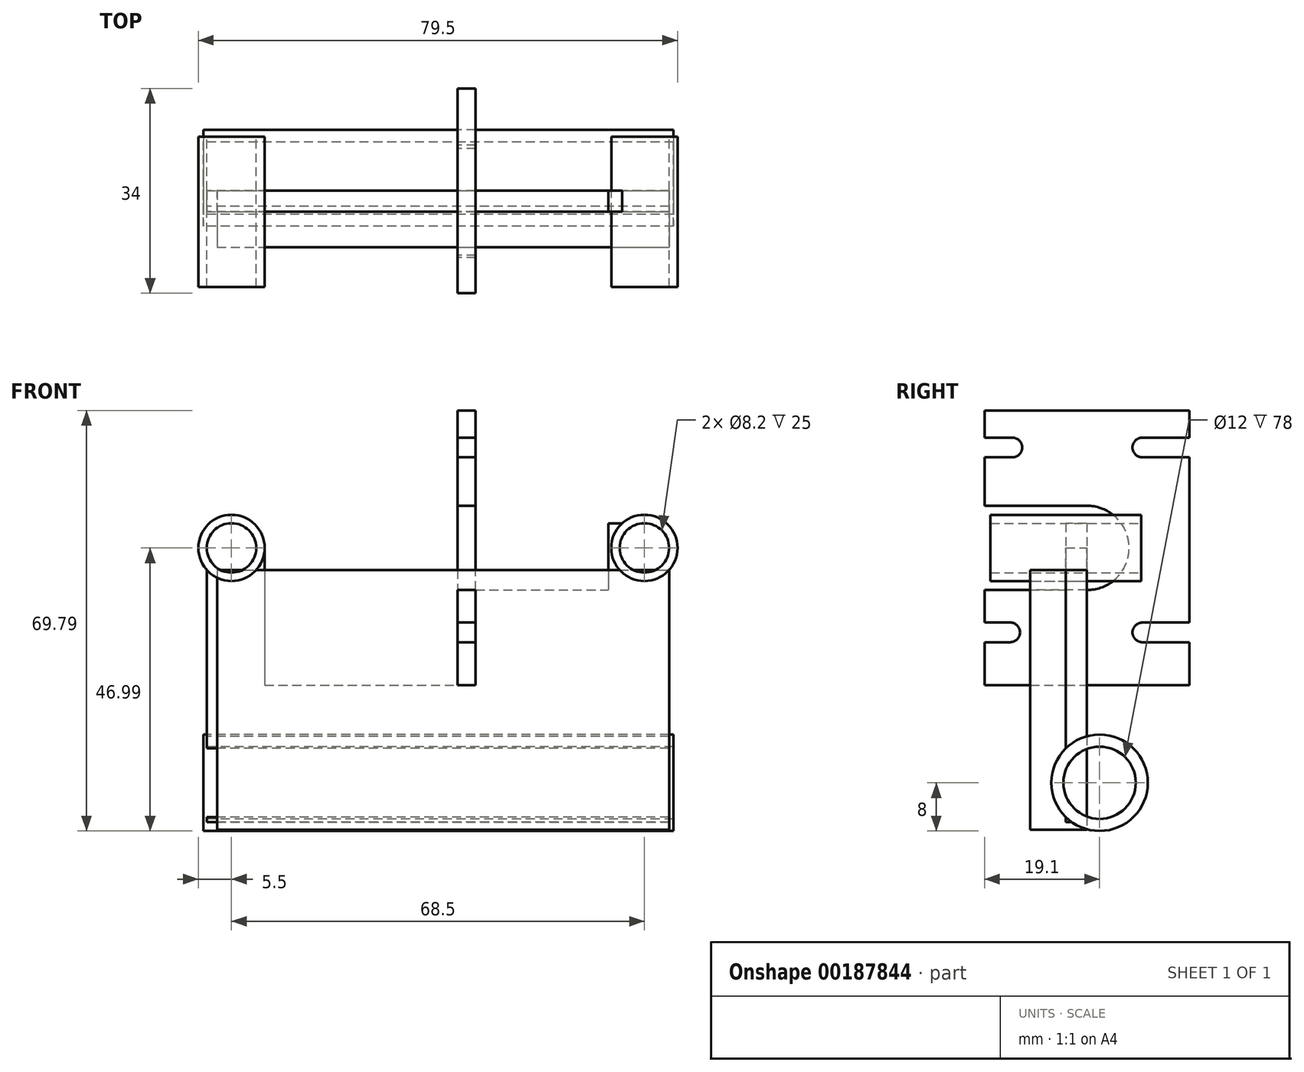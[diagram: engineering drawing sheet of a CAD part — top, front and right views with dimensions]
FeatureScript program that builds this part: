
annotation { "Feature Type Name" : "Feature", "Feature Type Description" : "" }
export const myFeature = defineFeature(function(context is Context, id is Id, definition is map)
    precondition{}
    {
        {
            var Q0;
            Q0=qCreatedBy(makeId("Front.planeOp"),FACE);
            var sketch = newSketch(context, id + "F0", { "sketchPlane" : qUnion([Q0])});
            skLineSegment(sketch, "E0.bottom", {"start": v(-35.33, 29.89) * mm, "end": v(33.17, 29.89) * mm});
            skLineSegment(sketch, "E0.top", {"start": v(-39.43, -19.7) * mm, "end": v(37.27, -19.7) * mm});
            skLineSegment(sketch, "E0.left", {"start": v(-39.43, 25.79) * mm, "end": v(-39.43, -19.7) * mm});
            skLineSegment(sketch, "E0.right", {"start": v(37.27, 25.79) * mm, "end": v(37.27, -19.7) * mm});
            skLineSegment(sketch, "E1", {"start": v(-46.82, 25.79) * mm, "end": v(49.11, 25.79) * mm, "construction": true});
            skCircle(sketch, "E2", {"center": v(-35.33, 25.79) * mm, "radius": 4.1 * mm});
            skCircle(sketch, "E3", {"center": v(33.17, 25.79) * mm, "radius": 4.1 * mm});
            skCircle(sketch, "E4", {"center": v(-35.33, 25.79) * mm, "radius": 5.5 * mm});
            skCircle(sketch, "E5", {"center": v(33.17, 25.79) * mm, "radius": 5.5 * mm});
            skLineSegment(sketch, "E6.top", {"start": v(2.17, 2.99) * mm, "end": v(-29.83, 2.99) * mm});
            skLineSegment(sketch, "E6.left", {"start": v(2.17, 48.59) * mm, "end": v(2.17, 2.99) * mm});
            skLineSegment(sketch, "E6.right", {"start": v(-29.83, 29.89) * mm, "end": v(-29.83, 2.99) * mm});
            skLineSegment(sketch, "E7.bottom", {"start": v(2.17, 48.59) * mm, "end": v(5.17, 48.59) * mm});
            skLineSegment(sketch, "E7.top", {"start": v(2.17, 2.99) * mm, "end": v(5.17, 2.99) * mm});
            skLineSegment(sketch, "E7.right", {"start": v(5.17, 48.59) * mm, "end": v(5.17, 2.99) * mm});
            skSolve(sketch);
        }
        {
            var Q0;
            {var subQ0=sQuery(id+"F0.wireOp",EDGE,"E2");var subQ1=sQuery(id+"F0.wireOp",EDGE,"E0.bottom");var subQ2=makeQuery(id+"F0.imprint","INTERSECT",VERTEX,{"derivedFrom":[subQ1,subQ0]});Q0=makeQuery(id+"F0.imprint","IMPRINT",FACE,{"disambiguationData":[TD([[makeQuery(id+"F0.imprint","IMPRINT",EDGE,{"disambiguationData":[TD([[subQ2,-1.0]])],"derivedFrom":subQ1}),1.0]])]});}
            var Q1;
            {var subQ1=sQuery(id+"F0.wireOp",EDGE,"E0.bottom");var subQ4=sQuery(id+"F0.wireOp",EDGE,"E2");var subQ5=makeQuery(id+"F0.imprint","INTERSECT",VERTEX,{"derivedFrom":[subQ1,subQ4]});Q1=makeQuery(id+"F0.imprint","IMPRINT",FACE,{"disambiguationData":[TD([[makeQuery(id+"F0.imprint","IMPRINT",EDGE,{"disambiguationData":[TD([[subQ5,-1.0]])],"derivedFrom":subQ1}),-1.0]])]});}
            var Q2;
            {var subQ0=sQuery(id+"F0.wireOp",EDGE,"E3");var subQ1=sQuery(id+"F0.wireOp",EDGE,"E0.bottom");var subQ2=makeQuery(id+"F0.imprint","INTERSECT",VERTEX,{"derivedFrom":[subQ1,subQ0]});Q2=makeQuery(id+"F0.imprint","IMPRINT",FACE,{"disambiguationData":[TD([[makeQuery(id+"F0.imprint","IMPRINT",EDGE,{"disambiguationData":[TD([[subQ2,1.0]])],"derivedFrom":subQ1}),1.0]])]});}
            var Q3;
            {var subQ0=sQuery(id+"F0.wireOp",EDGE,"E3");var subQ1=sQuery(id+"F0.wireOp",EDGE,"E0.bottom");var subQ2=makeQuery(id+"F0.imprint","INTERSECT",VERTEX,{"derivedFrom":[subQ1,subQ0]});Q3=makeQuery(id+"F0.imprint","IMPRINT",FACE,{"disambiguationData":[TD([[makeQuery(id+"F0.imprint","IMPRINT",EDGE,{"disambiguationData":[TD([[subQ2,1.0]])],"derivedFrom":subQ1}),-1.0]])]});}
            extrude(context, id + "F1", {"entities" : qUnion([Q0, Q1, Q2, Q3]), "depth" : 16 * mm, "hasSecondDirection" : true, "secondDirectionOppositeDirection" : true, "secondDirectionDepth" : 9 * mm});
        }
        {
            var Q0;
            {var subQ1=sQuery(id+"F0.wireOp",EDGE,"E0.top");Q0=makeQuery(id+"F0.imprint","IMPRINT",FACE,{"disambiguationData":[TD([[makeQuery(id+"F0.imprint","IMPRINT",EDGE,{"derivedFrom":subQ1}),1.0]])]});}
            extrude(context, id + "F2", {"entities" : qUnion([Q0]), "depth" : 3.5 * mm});
        }
        {
            var Q0;
            {var subQ5=sQuery(id+"F0.wireOp",EDGE,"E7.bottom");Q0=makeQuery(id+"F0.imprint","IMPRINT",FACE,{"disambiguationData":[TD([[makeQuery(id+"F0.imprint","IMPRINT",EDGE,{"derivedFrom":subQ5}),-1.0]])]});}
            var Q1;
            {var subQ5=sQuery(id+"F0.wireOp",EDGE,"E7.top");Q1=makeQuery(id+"F0.imprint","IMPRINT",FACE,{"disambiguationData":[TD([[makeQuery(id+"F0.imprint","IMPRINT",EDGE,{"derivedFrom":subQ5}),1.0]])]});}
            extrude(context, id + "F3", {"entities" : qUnion([Q0, Q1]), "operationType" : NewBodyOperationType.ADD, "depth" : 17 * mm, "hasSecondDirection" : true, "secondDirectionOppositeDirection" : true, "secondDirectionDepth" : 17 * mm});
        }
        {
            var Q0;
            Q0=makeQuery(id+"F3.opExtrude","SWEPT_FACE",FACE,{"disambiguationData":[OSD([sQuery(id+"F0.wireOp",EDGE,"E6.left")])]});
            var sketch = newSketch(context, id + "F4", { "sketchPlane" : qUnion([Q0])});
            skArc(sketch, "E8", {"start": v(0, 32.79) * mm, "mid": v(-7, 25.79) * mm, "end": v(0, 18.79) * mm});
            skPoint(sketch, "E8.centerSnap0", {"position": v(-17, 25.79) * mm});
            skPoint(sketch, "E8.centerSnap1", {"position": v(0, 48.59) * mm});
            skLineSegment(sketch, "E9.bottom", {"start": v(0, 32.79) * mm, "end": v(17, 32.79) * mm});
            skLineSegment(sketch, "E9.top", {"start": v(0, 18.79) * mm, "end": v(17, 18.79) * mm});
            skLineSegment(sketch, "E9.right", {"start": v(17, 32.79) * mm, "end": v(17, 18.79) * mm});
            skSolve(sketch);
        }
        {
            var Q0;
            Q0=makeQuery(id+"F4.imprint","IMPRINT",FACE,{"disambiguationData":[TD([[makeQuery(id+"F4.imprint","IMPRINT",EDGE,{"derivedFrom":sQuery(id+"F4.wireOp",EDGE,"E8")}),1.0]])]});
            extrude(context, id + "F5", {"entities" : qUnion([Q0]), "operationType" : NewBodyOperationType.REMOVE, "oppositeDirection" : true, "depth" : 25 * mm});
        }
        {
            var Q0;
            Q0=makeQuery(id+"F3.opExtrude","SWEPT_FACE",FACE,{"disambiguationData":[OSD([sQuery(id+"F0.wireOp",EDGE,"E6.left")])]});
            var sketch = newSketch(context, id + "F6", { "sketchPlane" : qUnion([Q0])});
            skArc(sketch, "E10", {"start": v(12.37, 44.09) * mm, "mid": v(10.74, 42.46) * mm, "end": v(12.37, 40.84) * mm});
            skArc(sketch, "E11", {"start": v(12.73, 13.4) * mm, "mid": v(11.1, 11.77) * mm, "end": v(12.73, 10.14) * mm});
            skArc(sketch, "E12", {"start": v(-9.18, 10.14) * mm, "mid": v(-7.55, 11.76) * mm, "end": v(-9.18, 13.39) * mm});
            skArc(sketch, "E13", {"start": v(-9.18, 40.84) * mm, "mid": v(-7.55, 42.46) * mm, "end": v(-9.18, 44.09) * mm});
            skLineSegment(sketch, "E14.bottom", {"start": v(12.37, 44.09) * mm, "end": v(18.8, 44.09) * mm});
            skLineSegment(sketch, "E14.top", {"start": v(12.37, 40.84) * mm, "end": v(18.8, 40.84) * mm});
            skLineSegment(sketch, "E14.right", {"start": v(18.8, 44.09) * mm, "end": v(18.8, 40.84) * mm});
            skLineSegment(sketch, "E15.bottom", {"start": v(-9.18, 44.09) * mm, "end": v(-17.68, 44.09) * mm});
            skLineSegment(sketch, "E15.top", {"start": v(-9.18, 40.84) * mm, "end": v(-17.68, 40.84) * mm});
            skLineSegment(sketch, "E15.right", {"start": v(-17.68, 44.09) * mm, "end": v(-17.68, 40.84) * mm});
            skLineSegment(sketch, "E16.bottom", {"start": v(-9.18, 13.39) * mm, "end": v(-21.31, 13.39) * mm});
            skLineSegment(sketch, "E16.top", {"start": v(-9.18, 10.14) * mm, "end": v(-21.31, 10.14) * mm});
            skLineSegment(sketch, "E16.right", {"start": v(-21.31, 13.39) * mm, "end": v(-21.31, 10.14) * mm});
            skLineSegment(sketch, "E17.bottom", {"start": v(12.73, 13.4) * mm, "end": v(20.87, 13.4) * mm});
            skLineSegment(sketch, "E17.top", {"start": v(12.73, 10.14) * mm, "end": v(20.87, 10.14) * mm});
            skLineSegment(sketch, "E17.right", {"start": v(20.87, 13.4) * mm, "end": v(20.87, 10.14) * mm});
            skSolve(sketch);
        }
        {
            var Q0;
            Q0=makeQuery(id+"F6.imprint","IMPRINT",FACE,{"disambiguationData":[TD([[makeQuery(id+"F6.imprint","IMPRINT",EDGE,{"derivedFrom":sQuery(id+"F6.wireOp",EDGE,"E13")}),1.0]])]});
            var Q1;
            Q1=makeQuery(id+"F6.imprint","IMPRINT",FACE,{"disambiguationData":[TD([[makeQuery(id+"F6.imprint","IMPRINT",EDGE,{"derivedFrom":sQuery(id+"F6.wireOp",EDGE,"E10")}),1.0]])]});
            var Q2;
            Q2=makeQuery(id+"F6.imprint","IMPRINT",FACE,{"disambiguationData":[TD([[makeQuery(id+"F6.imprint","IMPRINT",EDGE,{"derivedFrom":sQuery(id+"F6.wireOp",EDGE,"E11")}),1.0]])]});
            var Q3;
            Q3=makeQuery(id+"F6.imprint","IMPRINT",FACE,{"disambiguationData":[TD([[makeQuery(id+"F6.imprint","IMPRINT",EDGE,{"derivedFrom":sQuery(id+"F6.wireOp",EDGE,"E12")}),1.0]])]});
            extrude(context, id + "F7", {"entities" : qUnion([Q0, Q1, Q2, Q3]), "operationType" : NewBodyOperationType.REMOVE, "oppositeDirection" : true, "depth" : 25 * mm});
        }
        {
            var Q0;
            Q0=qCreatedBy(makeId("Right.planeOp"),FACE);
            var sketch = newSketch(context, id + "F8", { "sketchPlane" : qUnion([Q0])});
            skCircle(sketch, "E18", {"center": v(2.1, -13.2) * mm, "radius": 6 * mm});
            skCircle(sketch, "E19", {"center": v(2.1, -13.2) * mm, "radius": 8 * mm});
            skPoint(sketch, "E20.orphan", {"position": v(-3.38, -13.2) * mm});
            skPoint(sketch, "E21.orphan", {"position": v(7.6, -13.2) * mm});
            skSolve(sketch);
        }
        {
            var Q0;
            {var subQ4=sQuery(id+"F0.wireOp",EDGE,"E5");var subQ6=sQuery(id+"F0.wireOp",EDGE,"E0.right");Q0=makeQuery(id+"F10.boolean.opBoolean","SPLIT",FACE,{"disambiguationData":[TD([makeQuery(id+"F2.opExtrude","SWEPT_FACE",FACE,{"disambiguationData":[OSD([subQ4])]})])],"derivedFrom":makeQuery(id+"F2.opExtrude","SWEPT_FACE",FACE,{"disambiguationData":[OSD([subQ6])]})});}
            var sketch = newSketch(context, id + "F9", { "sketchPlane" : qUnion([Q0])});
            skLineSegment(sketch, "E22.bottom", {"start": v(0, 22.12) * mm, "end": v(-9.4, 22.12) * mm});
            skLineSegment(sketch, "E22.top", {"start": v(0, -21) * mm, "end": v(-9.4, -21) * mm});
            skLineSegment(sketch, "E22.left", {"start": v(0, 22.12) * mm, "end": v(0, -21) * mm});
            skLineSegment(sketch, "E22.right", {"start": v(-9.4, 22.12) * mm, "end": v(-9.4, -21) * mm});
            skSolve(sketch);
        }
        {
            var Q0;
            Q0=makeQuery(id+"F8.imprint","IMPRINT",FACE,{"disambiguationData":[TD([[makeQuery(id+"F8.imprint","IMPRINT",EDGE,{"derivedFrom":sQuery(id+"F8.wireOp",EDGE,"E18")}),-1.0]])]});
            extrude(context, id + "F10", {"entities" : qUnion([Q0]), "operationType" : NewBodyOperationType.ADD, "depth" : 38 * mm, "hasSecondDirection" : true, "secondDirectionOppositeDirection" : true, "secondDirectionDepth" : 40 * mm});
        }
        {
            var Q0;
            Q0=makeQuery(id+"F8.imprint","IMPRINT",FACE,{"disambiguationData":[TD([[makeQuery(id+"F8.imprint","IMPRINT",EDGE,{"derivedFrom":sQuery(id+"F8.wireOp",EDGE,"E18")}),1.0]])]});
            extrude(context, id + "F11", {"entities" : qUnion([Q0]), "operationType" : NewBodyOperationType.REMOVE, "endBound" : BoundingType.THROUGH_ALL, "oppositeDirection" : true, "depth" : 40 * mm, "hasSecondDirection" : true, "secondDirectionOppositeDirection" : false, "secondDirectionDepth" : 40 * mm});
        }
        {
            var Q0;
            {var subQ3=sQuery(id+"F0.wireOp",EDGE,"E0.right");var subQ4=makeQuery(id+"F2.opExtrude","CAP_EDGE",EDGE,{"disambiguationData":[OSD([subQ3])],"isStart":false});Q0=makeQuery(id+"F9.imprint","IMPRINT",FACE,{"disambiguationData":[TD([[makeQuery(id+"F9.imprint","IMPRINT",EDGE,{"derivedFrom":subQ4}),1.0]])]});}
            var Q1;
            {var subQ4=sQuery(id+"F9.wireOp",EDGE,"E22.top");Q1=makeQuery(id+"F9.imprint","IMPRINT",FACE,{"disambiguationData":[TD([[makeQuery(id+"F9.imprint","IMPRINT",EDGE,{"derivedFrom":subQ4}),-1.0]])]});}
            extrude(context, id + "F12", {"entities" : qUnion([Q0, Q1]), "oppositeDirection" : true, "depth" : 75 * mm});
        }
    });
